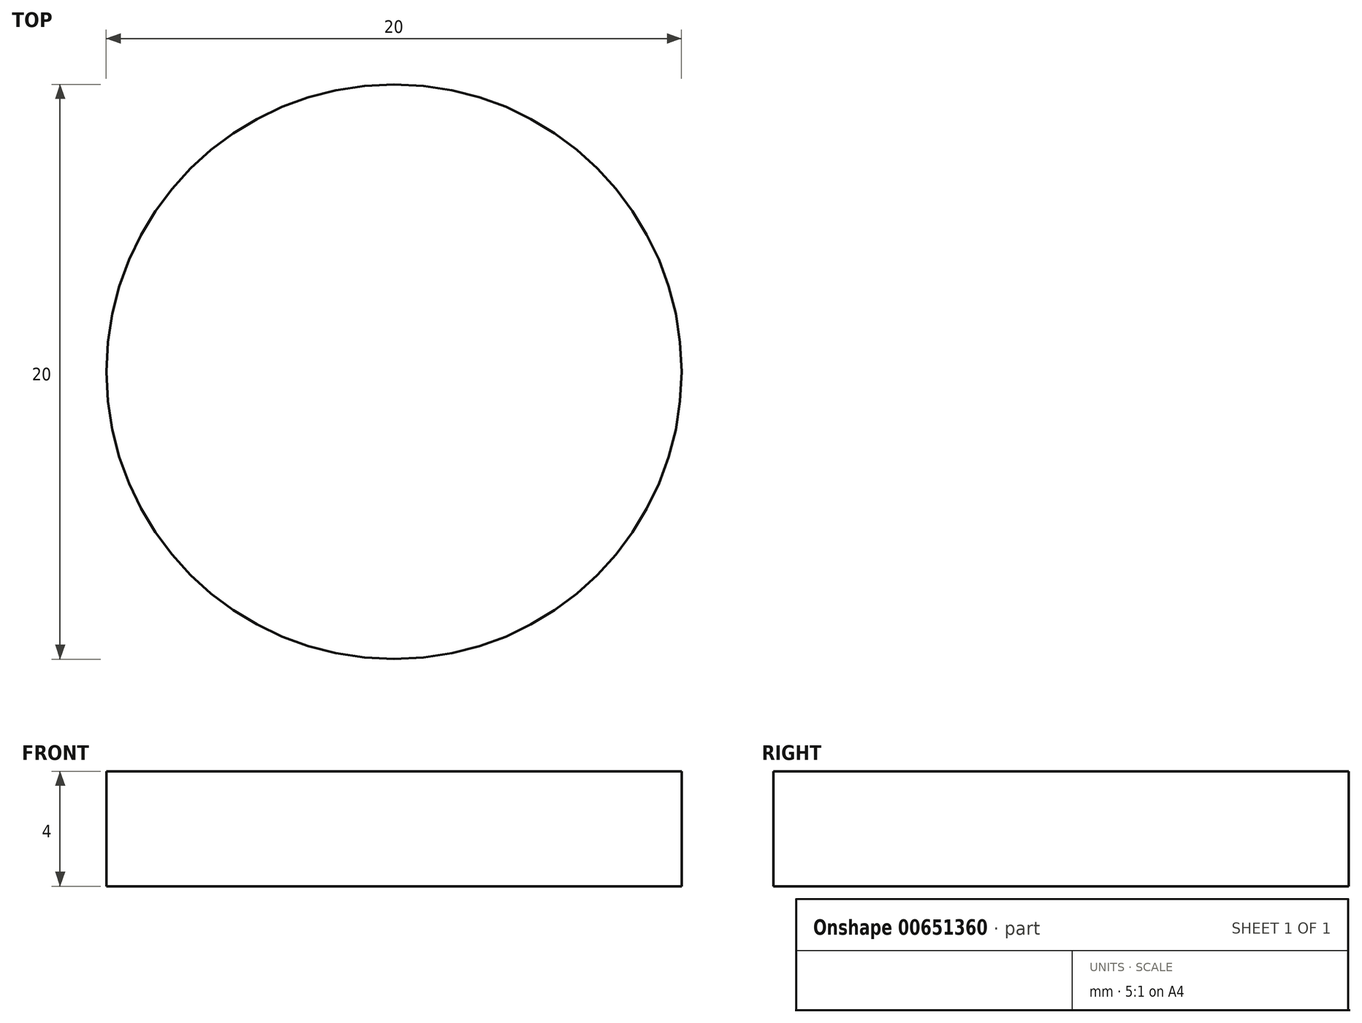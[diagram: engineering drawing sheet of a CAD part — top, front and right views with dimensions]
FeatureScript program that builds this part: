
annotation { "Feature Type Name" : "Feature", "Feature Type Description" : "" }
export const myFeature = defineFeature(function(context is Context, id is Id, definition is map)
    precondition{}
    {
        {
            var Q0;
            Q0=qCreatedBy(makeId("Top.planeOp"),FACE);
            var sketch = newSketch(context, id + "F0", { "sketchPlane" : qUnion([Q0])});
            skCircle(sketch, "E0", {"center": v(-18.12, 19.91) * mm, "radius": 10 * mm});
            skSolve(sketch);
        }
        {
            var Q0;
            Q0=makeQuery(id+"F0.imprint","IMPRINT",FACE,{"disambiguationData":[TD([[makeQuery(id+"F0.imprint","IMPRINT",EDGE,{"derivedFrom":sQuery(id+"F0.wireOp",EDGE,"E0")}),1.0]])]});
            extrude(context, id + "F1", {"entities" : qUnion([Q0]), "depth" : 4 * mm, "offsetDistance" : 25 * mm});
        }
    });
